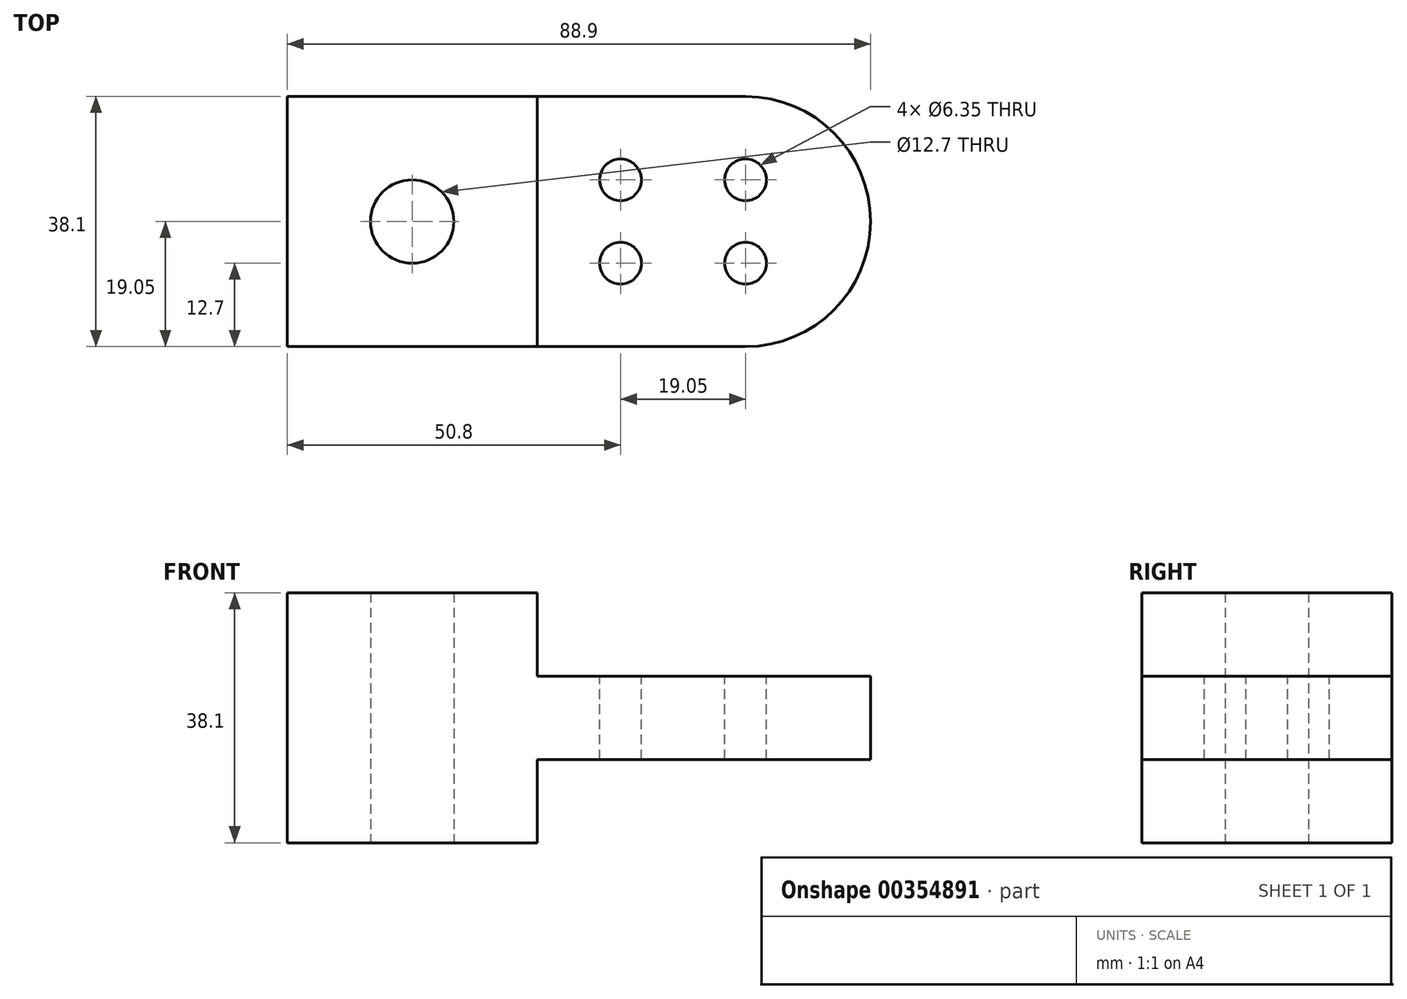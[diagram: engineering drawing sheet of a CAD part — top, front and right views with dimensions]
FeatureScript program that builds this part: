
annotation { "Feature Type Name" : "Feature", "Feature Type Description" : "" }
export const myFeature = defineFeature(function(context is Context, id is Id, definition is map)
    precondition{}
    {
        {
            var Q0;
            Q0=qCreatedBy(makeId("Top.planeOp"),FACE);
            var sketch = newSketch(context, id + "F0", { "sketchPlane" : qUnion([Q0])});
            skLineSegment(sketch, "E0.bottom", {"start": v(0, 19.05) * mm, "end": v(38.1, 19.05) * mm});
            skLineSegment(sketch, "E0.top", {"start": v(0, -19.05) * mm, "end": v(38.1, -19.05) * mm});
            skLineSegment(sketch, "E0.left", {"start": v(0, 19.05) * mm, "end": v(0, -19.05) * mm});
            skLineSegment(sketch, "E0.right", {"start": v(38.1, 19.05) * mm, "end": v(38.1, -19.05) * mm});
            skCircle(sketch, "E1", {"center": v(19.05, 0) * mm, "radius": 6.35 * mm});
            skPoint(sketch, "E1.centerSnap0", {"position": v(38.1, 0) * mm});
            skSolve(sketch);
        }
        {
            var Q0;
            Q0 = qSketchRegion(id + "F0", true);
            extrude(context, id + "F1", {"entities" : qUnion([Q0]), "endBound" : BoundingType.SYMMETRIC, "depth" : 38.1 * mm});
        }
        {
            var Q0;
            Q0=makeQuery(id+"F1.opExtrude","SWEPT_FACE",FACE,{"disambiguationData":[OSD([sQuery(id+"F0.wireOp",EDGE,"E0.right")])]});
            var sketch = newSketch(context, id + "F2", { "sketchPlane" : qUnion([Q0])});
            skLineSegment(sketch, "E2.bottom", {"start": v(-19.05, -6.35) * mm, "end": v(19.05, -6.35) * mm});
            skLineSegment(sketch, "E2.top", {"start": v(-19.05, 6.35) * mm, "end": v(19.05, 6.35) * mm});
            skLineSegment(sketch, "E2.left", {"start": v(-19.05, -6.35) * mm, "end": v(-19.05, 6.35) * mm});
            skLineSegment(sketch, "E2.right", {"start": v(19.05, -6.35) * mm, "end": v(19.05, 6.35) * mm});
            skSolve(sketch);
        }
        {
            var Q0;
            Q0 = qSketchRegion(id + "F2", true);
            extrude(context, id + "F3", {"entities" : qUnion([Q0]), "operationType" : NewBodyOperationType.ADD, "depth" : 31.75 * mm});
        }
        {
            var Q0;
            Q0=makeQuery(id+"F3.opExtrude","SWEPT_FACE",FACE,{"disambiguationData":[OSD([sQuery(id+"F2.wireOp",EDGE,"E2.top")])]});
            var sketch = newSketch(context, id + "F4", { "sketchPlane" : qUnion([Q0])});
            skArc(sketch, "E3", {"start": v(69.85, -19.05) * mm, "mid": v(88.9, 0) * mm, "end": v(69.85, 19.05) * mm});
            skSolve(sketch);
        }
        {
            var Q0;
            Q0=makeQuery(id+"F4.imprint","IMPRINT",FACE,{"disambiguationData":[TD([[makeQuery(id+"F4.imprint","IMPRINT",EDGE,{"derivedFrom":sQuery(id+"F4.wireOp",EDGE,"E3")}),1.0]])]});
            extrude(context, id + "F5", {"entities" : qUnion([Q0]), "operationType" : NewBodyOperationType.ADD, "oppositeDirection" : true, "depth" : 12.7 * mm});
        }
        {
            var Q0;
            {var subQ0=sQuery(id+"F2.wireOp",EDGE,"E2.top");Q0=makeQuery(id+"F5.boolean.opBoolean","MERGE",FACE,{"derivedFrom":[makeQuery(id+"F3.opExtrude","SWEPT_FACE",FACE,{"disambiguationData":[OSD([subQ0])]}),makeQuery(id+"F5.opExtrude","CAP_FACE",FACE,{"disambiguationData":[OSD([subQ0,sQuery(id+"F4.wireOp",EDGE,"E3")])],"isStart":true})]});}
            var sketch = newSketch(context, id + "F6", { "sketchPlane" : qUnion([Q0])});
            skLineSegment(sketch, "E4.bottom", {"start": v(50.8, 6.35) * mm, "end": v(69.85, 6.35) * mm, "construction": true});
            skLineSegment(sketch, "E4.top", {"start": v(50.8, -6.35) * mm, "end": v(69.85, -6.35) * mm, "construction": true});
            skLineSegment(sketch, "E4.left", {"start": v(50.8, 6.35) * mm, "end": v(50.8, -6.35) * mm, "construction": true});
            skLineSegment(sketch, "E4.right", {"start": v(69.85, 6.35) * mm, "end": v(69.85, -6.35) * mm, "construction": true});
            skCircle(sketch, "E5", {"center": v(50.8, 6.35) * mm, "radius": 3.18 * mm});
            skCircle(sketch, "E6", {"center": v(50.8, -6.35) * mm, "radius": 3.18 * mm});
            skCircle(sketch, "E7", {"center": v(69.85, 6.35) * mm, "radius": 3.18 * mm});
            skCircle(sketch, "E8", {"center": v(69.85, -6.35) * mm, "radius": 3.18 * mm});
            skSolve(sketch);
        }
        {
            var Q0;
            Q0 = qSketchRegion(id + "F6", true);
            extrude(context, id + "F7", {"entities" : qUnion([Q0]), "operationType" : NewBodyOperationType.REMOVE, "oppositeDirection" : true, "depth" : 25.4 * mm});
        }
    });
